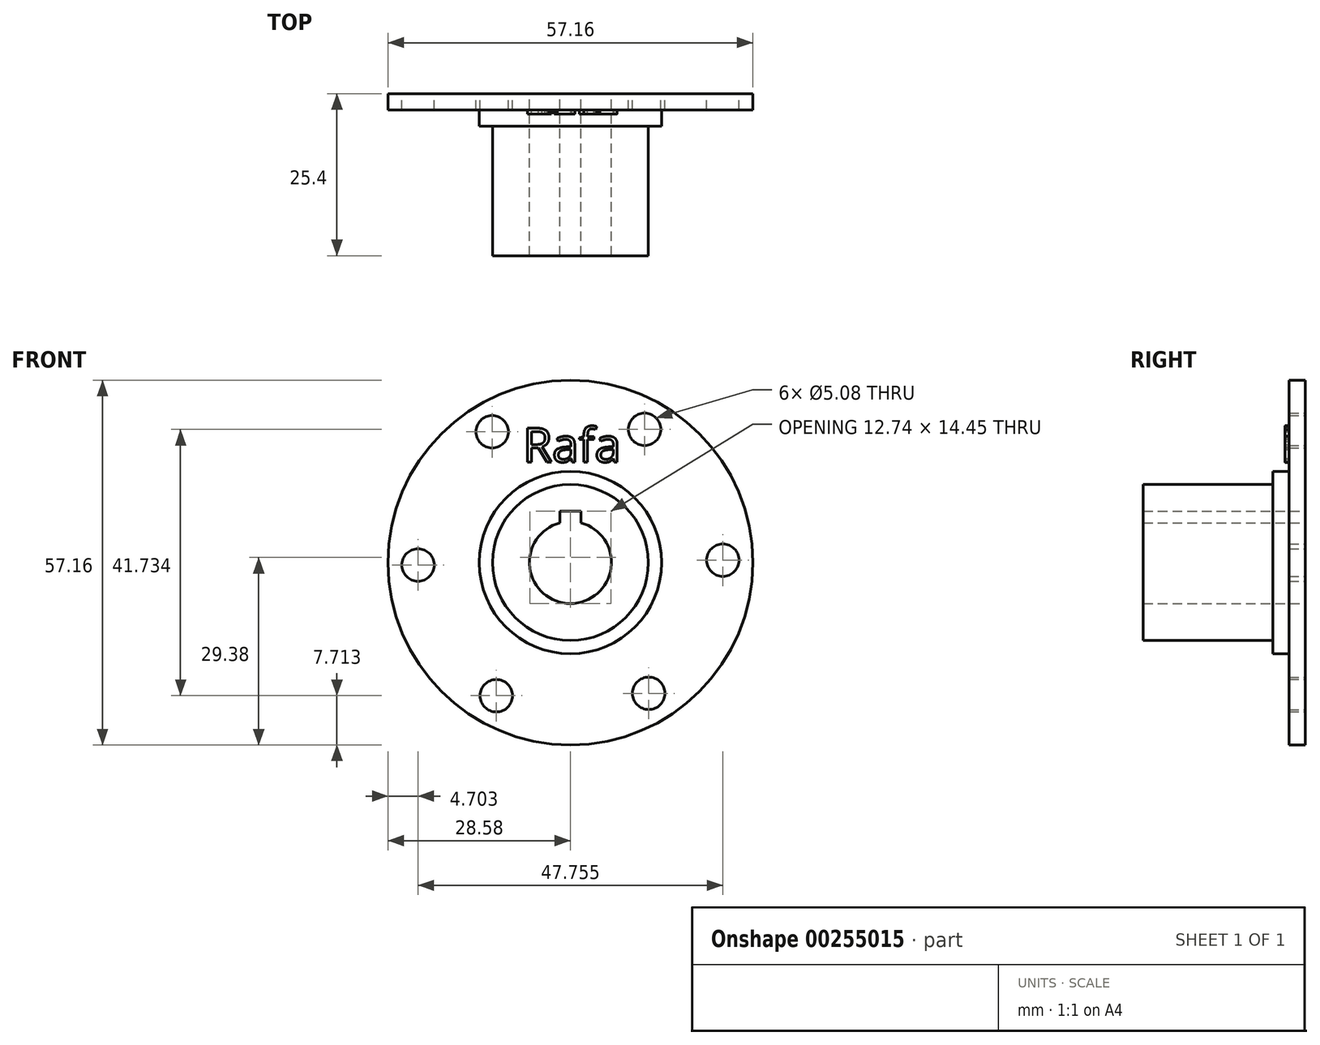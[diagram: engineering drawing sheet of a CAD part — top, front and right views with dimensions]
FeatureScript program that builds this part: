
annotation { "Feature Type Name" : "Feature", "Feature Type Description" : "" }
export const myFeature = defineFeature(function(context is Context, id is Id, definition is map)
    precondition{}
    {
        {
            var Q0;
            Q0=qCreatedBy(makeId("Front.planeOp"),FACE);
            var sketch = newSketch(context, id + "F0", { "sketchPlane" : qUnion([Q0])});
            skCircle(sketch, "E0", {"center": v(0, 0) * mm, "radius": 28.58 * mm});
            skArc(sketch, "E1", {"start": v(-12.13, 20.5) * mm, "mid": v(-12.23, 20.43) * mm, "end": v(-12.33, 20.37) * mm});
            skLineSegment(sketch, "E2.0", {"start": v(-23.88, -0.38) * mm, "end": v(-23.81, -0.26) * mm});
            skLineSegment(sketch, "E2.1", {"start": v(-12.27, 20.49) * mm, "end": v(-12.13, 20.5) * mm});
            skLineSegment(sketch, "E2.2", {"start": v(11.61, 20.87) * mm, "end": v(11.68, 20.75) * mm});
            skLineSegment(sketch, "E2.3", {"start": v(23.88, 0.38) * mm, "end": v(23.81, 0.26) * mm});
            skLineSegment(sketch, "E2.4", {"start": v(12.27, -20.49) * mm, "end": v(12.13, -20.5) * mm});
            skLineSegment(sketch, "E2.5", {"start": v(-11.61, -20.87) * mm, "end": v(-11.68, -20.75) * mm});
            skCircle(sketch, "E3", {"center": v(-12.27, 20.49) * mm, "radius": 2.54 * mm});
            skCircle(sketch, "E4", {"center": v(11.61, 20.87) * mm, "radius": 2.54 * mm});
            skCircle(sketch, "E5", {"center": v(23.88, 0.38) * mm, "radius": 2.54 * mm});
            skCircle(sketch, "E6", {"center": v(12.27, -20.49) * mm, "radius": 2.54 * mm});
            skCircle(sketch, "E7", {"center": v(-11.61, -20.87) * mm, "radius": 2.54 * mm});
            skCircle(sketch, "E8", {"center": v(-23.88, -0.38) * mm, "radius": 2.54 * mm});
            skLineSegment(sketch, "E9.trimOffspring", {"start": v(11.48, 20.86) * mm, "end": v(11.61, 20.87) * mm});
            skLineSegment(sketch, "E10.trimOffspring", {"start": v(-12.33, 20.37) * mm, "end": v(-12.27, 20.49) * mm});
            skLineSegment(sketch, "E11.trimOffspring", {"start": v(23.8, 0.5) * mm, "end": v(23.88, 0.38) * mm});
            skLineSegment(sketch, "E12.trimOffspring", {"start": v(-23.8, -0.5) * mm, "end": v(-23.88, -0.38) * mm});
            skLineSegment(sketch, "E13.trimOffspring", {"start": v(-11.48, -20.86) * mm, "end": v(-11.61, -20.87) * mm});
            skLineSegment(sketch, "E14.trimOffspring", {"start": v(12.33, -20.37) * mm, "end": v(12.27, -20.49) * mm});
            skCircle(sketch, "E15", {"center": v(0, 0) * mm, "radius": 14.29 * mm});
            skCircle(sketch, "E16", {"center": v(0, 0) * mm, "radius": 12.22 * mm});
            skArc(sketch, "E17", {"start": v(-1.65, 6.21) * mm, "mid": v(0, -6.43) * mm, "end": v(1.65, 6.21) * mm});
            skLineSegment(sketch, "E18.bottom", {"start": v(-1.65, 8.03) * mm, "end": v(1.65, 8.03) * mm});
            skLineSegment(sketch, "E18.left", {"start": v(-1.65, 8.03) * mm, "end": v(-1.65, 6.21) * mm});
            skLineSegment(sketch, "E18.right", {"start": v(1.65, 8.03) * mm, "end": v(1.65, 6.21) * mm});
            skArc(sketch, "E19.trimOffspring", {"start": v(-23.81, -0.26) * mm, "mid": v(-23.8, -0.38) * mm, "end": v(-23.8, -0.5) * mm});
            skArc(sketch, "E20.trimOffspring", {"start": v(-11.68, -20.75) * mm, "mid": v(-11.58, -20.8) * mm, "end": v(-11.48, -20.86) * mm});
            skArc(sketch, "E21.trimOffspring", {"start": v(12.13, -20.5) * mm, "mid": v(12.23, -20.43) * mm, "end": v(12.33, -20.37) * mm});
            skArc(sketch, "E22.trimOffspring", {"start": v(23.81, 0.26) * mm, "mid": v(23.8, 0.38) * mm, "end": v(23.8, 0.5) * mm});
            skArc(sketch, "E23.trimOffspring", {"start": v(11.68, 20.75) * mm, "mid": v(11.58, 20.8) * mm, "end": v(11.48, 20.86) * mm});
            skSolve(sketch);
        }
        {
            var Q0;
            Q0=makeQuery(id+"F0.imprint","IMPRINT",FACE,{"disambiguationData":[TD([[makeQuery(id+"F0.imprint","IMPRINT",EDGE,{"derivedFrom":sQuery(id+"F0.wireOp",EDGE,"E0")}),1.0]])]});
            var Q1;
            Q1=makeQuery(id+"F0.imprint","IMPRINT",FACE,{"disambiguationData":[TD([[makeQuery(id+"F0.imprint","IMPRINT",EDGE,{"derivedFrom":sQuery(id+"F0.wireOp",EDGE,"E15")}),-1.0]])]});
            extrude(context, id + "F1", {"entities" : qUnion([Q0, Q1]), "depth" : 2.54 * mm});
        }
        {
            var Q0;
            Q0=makeQuery(id+"F0.imprint","IMPRINT",FACE,{"disambiguationData":[TD([[makeQuery(id+"F0.imprint","IMPRINT",EDGE,{"derivedFrom":sQuery(id+"F0.wireOp",EDGE,"E15")}),1.0]])]});
            extrude(context, id + "F2", {"entities" : qUnion([Q0]), "operationType" : NewBodyOperationType.ADD, "depth" : 5.08 * mm});
        }
        {
            var Q0;
            Q0=makeQuery(id+"F0.imprint","IMPRINT",FACE,{"disambiguationData":[TD([[makeQuery(id+"F0.imprint","IMPRINT",EDGE,{"derivedFrom":sQuery(id+"F0.wireOp",EDGE,"E16")}),1.0]])]});
            extrude(context, id + "F3", {"entities" : qUnion([Q0]), "operationType" : NewBodyOperationType.ADD, "depth" : 25.4 * mm});
        }
        {
            var Q0;
            Q0=qCreatedBy(makeId("Front.planeOp"),FACE);
            var sketch = newSketch(context, id + "F4", { "sketchPlane" : qUnion([Q0])});
            skText(sketch, "E24", { "text": "Rafa", "fontName": "OpenSans-Regular.ttf"});
            const initialGuessF4  = {"E24": [-0.00745, 0.01576, 1, 0, 0.00535]};
            skSetInitialGuess(sketch, initialGuessF4);
            skSolve(sketch);
        }
        {
            var Q0;
            Q0 = qSketchRegion(id + "F4", true);
            extrude(context, id + "F5", {"entities" : qUnion([Q0]), "operationType" : NewBodyOperationType.ADD, "depth" : 3.17 * mm});
        }
    });
